# Revit family: BSC-Class-II_Type-A2_NuAire_Cellgard_475-477
name_source: partatom
category: Mechanical Equipment
units: mm (PartAtom-declared; Revit-internal decimal feet)

## family parameters
Always vertical = Yes
Classification Number = 23.40.70.11.11.11.11
Cut with Voids When Loaded = No
Maintain Annotation Orientation = No
Part Type = Normal
Room Calculation Point = No
Round Connector Dimension = Use Diameter
Shared = No
Work Plane-Based = No

## types (16) — shared parameters
Assembly Code = E1020720
Construction Details = http://www.arcat.com
DEPTH = 2' - 7 19/32"
Default Elevation = 0' - 0"
Description = Class II Type A2 Biological Safety Cabinet
HEIGHT = 4' - 10 7/8"
Keynote = 11 53 00
Manufacturer = Nuaire Inc
Manufacturer Fax = 763-553-0459
Manufacturer Website = http://www.nuaire.com
Product Data = http://www.arcat.com
Product Properties = http://www.nuaire.com
Revision = R1_12/2015
Sales Information = http://www.nuaire.com
Specification = http://www.arcat.com
Type Comments = Contact Sales for Info: 800-328-3352, 888-4-NUAIRE, www.nuaire.com
URL = http://www.nuaire.com
WIDTH = 6' - 5 13/16"
WORK SURFACE HEIGHT = 2' - 8 5/8"

## per-type parameters (varying)
| type | Model |
| NU-475-300 - 30 Work Surface Height | NU-475-300 |
| NU-475-500 - 36 Work Surface Height | NU-475-500 |
| NU-475-600 - 30 Work Surface Height | NU-475-600 |
| NU-475-300 - 36 Work Surface Height | NU-475-300 |
| NU-475-400 - 36 Work Surface Height | NU-475-400 |
| NU-475-600 - 36 Work Surface Height | NU-475-600 |
| NU-475-500 - 30 Work Surface Height | NU-475-500 |
| NU-475-400 - 30 Work Surface Height | NU-475-300 |
| NU-477-300 - 30 Work Surface Height | NU-477-300 |
| NU-477-500 - 36 Work Surface Height | NU-477-500 |
| NU-477-600 - 30 Work Surface Height | NU-477-600 |
| NU-477-300 - 36 Work Surface Height | NU-477-300 |
| NU-477-400 - 36 Work Surface Height | NU-477-400 |
| NU-477-600 - 36 Work Surface Height | NU-477-600 |
| NU-477-500 - 30 Work Surface Height | NU-477-500 |
| NU-477-400 - 30 Work Surface Height | NU-477-300 |

## geometry (parser evidence)
native form markers: Blend x10, Sweep x3
no freeform markers — native parametric forms only
